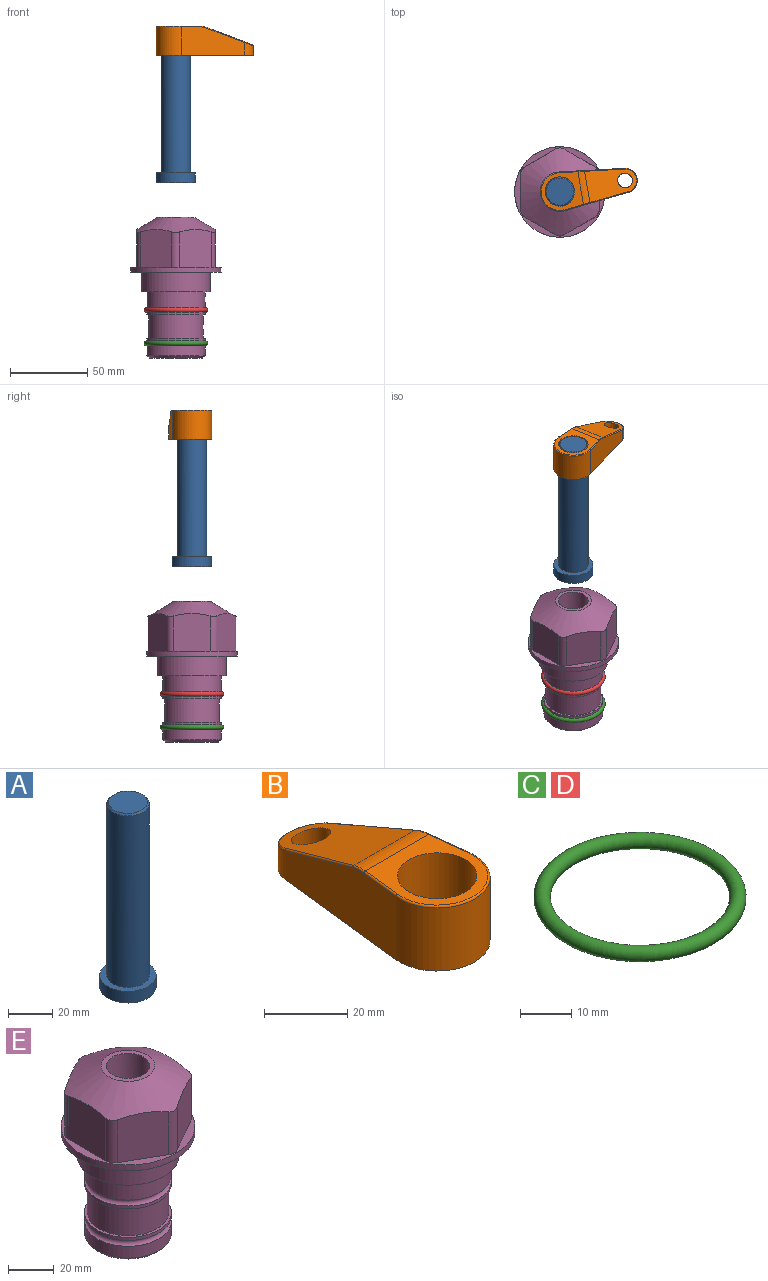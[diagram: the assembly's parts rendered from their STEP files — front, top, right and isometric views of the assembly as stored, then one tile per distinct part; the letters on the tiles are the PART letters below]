
ASSEMBLY  parts=5 mates=3
PART A: 6 faces, bbox 25.4x25.4x101.6 mm
  f0: plane 17.46x17.46mm, normal (0,0,1), area 239.5mm2, adj f5
  f1: plane 25.4x25.4mm, normal (0,0,-1), area 506.7mm2, adj f2
  f2: cylinder r=12.7mm len=25.4mm, axis (0,0,1), area 506.7mm2, adj f1,f3
  f3: plane 25.4x25.4mm, normal (0,0,1), area 221.7mm2, adj f2,f4
  f4: cylinder r=9.53mm len=94.46mm, axis (0,0,1), area 5653mm2, adj f3,f5
  f5: cone r=8.73mm half-angle=45deg, axis (0,0,-1), area 64.4mm2, adj f0,f4
PART B: 44 faces, bbox 27.5x64.5x19.1 mm
  f0: plane 2.3x0.95mm, normal (0,0,-1), area 1mm2, adj f25,f30,f34
  f1: plane 63.5x25.4mm, normal (0,0,-1), area 561.7mm2, adj f2,f3,f4,f5,f6,f7,f19,f20
  f2: cylinder r=12.7mm len=25.4mm, axis (0,0,-1), area 792.2mm2, adj f1,f3,f5,f13
  f3: plane 42.33x18.54mm, normal (0.99,0.11,0), area 647mm2, adj f1,f2,f4,f11,f12,f14
  f4: cylinder r=7.94mm len=15.78mm, axis (0,0,-1), area 158.6mm2, adj f1,f3,f5,f16
  f5: plane 42.33x18.54mm, normal (-0.99,0.11,0), area 647mm2, adj f1,f2,f4,f15,f17,f18
  f6: cylinder r=9.53mm len=19.05mm, axis (0,0,-1), area 1140.1mm2, adj f1,f8
  f7: cylinder r=4.76mm len=10.98mm, axis (0,0,-1), area 276.1mm2, adj f1,f9
  f8: plane 25.83x24.38mm, normal (0,0,1), area 262.2mm2, adj f6,f10,f11,f13,f15
  f9: plane 32.49x20.55mm, normal (0,0.34,0.94), area 489.9mm2, adj f7,f10,f14,f16,f18
  f10: cylinder r=12.7mm len=21.49mm, axis (-1,0,0), area 93.2mm2, adj f8,f9,f12,f17
  f11: cylinder r=0.51mm len=12.34mm, axis (0.11,-0.99,0), area 9.9mm2, adj f3,f8,f12,f13
  f12: bspline ~7.62x1.64mm, area 3.5mm2, adj f3,f10,f11,f14
  f13: torus R=12.19mm, axis (0,0,1), area 33.6mm2, adj f2,f8,f11,f15
  f14: cylinder r=0.51mm len=26.01mm, axis (0.1,-0.93,0.34), area 21.6mm2, adj f3,f9,f12,f16
  f15: cylinder r=0.51mm len=12.34mm, axis (0.11,0.99,0), area 9.9mm2, adj f5,f8,f13,f17
  f16: bspline ~15.78x7.05mm, area 15.7mm2, adj f4,f9,f14,f18
  f17: bspline ~7.62x1.64mm, area 3.5mm2, adj f5,f10,f15,f18
  f18: cylinder r=0.51mm len=26.01mm, axis (0.1,0.93,-0.34), area 21.6mm2, adj f5,f9,f16,f17
  f19: plane 21.6x14.29mm, normal (-0.99,-0.11,0), area 242.6mm2, adj f1,f26,f28,f34,f36,f38
  f20: plane 21.6x14.29mm, normal (0.99,-0.11,0), area 242.6mm2, adj f1,f27,f29,f37,f39,f41
  f21: cylinder r=12.7mm len=14.29mm, axis (0,0,-1), area 173.2mm2, adj f1,f26,f27,f30,f31,f33
  f22: cylinder r=7.94mm len=7.63mm, axis (0,0,-1), area 53.8mm2, adj f1,f28,f29,f42
  f23: plane 2.3x0.95mm, normal (0,0,-1), area 1mm2, adj f25,f33,f37
  f24: plane 17.94x12.32mm, normal (0,-0.34,-0.94), area 191.2mm2, adj f25,f38,f41,f42
  f25: cylinder r=9.53mm len=12.93mm, axis (-1,0,0), area 37.5mm2, adj f0,f23,f24,f31,f36,f39
  f26: cylinder r=1.59mm len=14.29mm, axis (0,0,-1), area 49mm2, adj f1,f19,f21,f32
  f27: cylinder r=1.59mm len=14.29mm, axis (0,0,-1), area 49mm2, adj f1,f20,f21,f35
  f28: cylinder r=1.59mm len=7.28mm, axis (0,0,-1), area 22.1mm2, adj f1,f19,f22,f40
  f29: cylinder r=1.59mm len=7.28mm, axis (0,0,-1), area 22.1mm2, adj f1,f20,f22,f43
  f30: torus R=14.29mm, axis (0,0,1), area 5.8mm2, adj f0,f21,f31,f32
  f31: bspline ~11.06x2.73mm, area 20.8mm2, adj f21,f25,f30,f33
  f32: sphere r=1.59mm, area 5.4mm2, adj f26,f30,f34
  f33: torus R=14.29mm, axis (0,0,1), area 5.8mm2, adj f21,f23,f31,f35
  f34: cylinder r=1.59mm len=1.68mm, axis (-0.11,0.99,0), area 2.4mm2, adj f0,f19,f32,f36
  f35: sphere r=1.59mm, area 5.4mm2, adj f27,f33,f37
  f36: bspline ~5.82x2.33mm, area 7.7mm2, adj f19,f25,f34,f38
  f37: cylinder r=1.59mm len=1.68mm, axis (0.11,0.99,0), area 2.4mm2, adj f20,f23,f35,f39
  f38: cylinder r=1.59mm len=18.33mm, axis (0.1,-0.93,0.34), area 46.7mm2, adj f19,f24,f36,f40
  f39: bspline ~5.82x2.33mm, area 7.7mm2, adj f20,f25,f37,f41
  f40: sphere r=1.59mm, area 3.6mm2, adj f28,f38,f42
  f41: cylinder r=1.59mm len=18.33mm, axis (0.1,0.93,-0.34), area 46.7mm2, adj f20,f24,f39,f43
  f42: bspline ~8.31x1.84mm, area 15.3mm2, adj f22,f24,f40,f43
  f43: sphere r=1.59mm, area 3.6mm2, adj f29,f41,f42
PART C: 1 faces, bbox 44.7x44.7x3.2 mm
  f0: torus R=19.05mm, axis (0,0,1), area 1193.9mm2
PART D: same geometry as C
PART E: 36 faces, bbox 58.7x58.7x91.2 mm
  f0: cylinder r=17.78mm len=35.56mm, axis (0,0,1), area 1670.8mm2, adj f23,f24,f31
  f1: cylinder r=19.05mm len=38.1mm, axis (0,0,1), area 1191.9mm2, adj f26,f27,f30
  f2: plane 58.66x58.66mm, normal (0,0,-1), area 1150.6mm2, adj f3,f28
  f3: cylinder r=29.33mm len=58.66mm, axis (0,0,-1), area 585.1mm2, adj f2,f4
  f4: plane 58.66x58.66mm, normal (0,0,1), area 475.9mm2, adj f3,f5,f6,f7,f8,f9,f10,f11
  f5: plane 24.5x20.32mm, normal (0.5,-0.87,0), area 562.8mm2, adj f4,f15,f16,f17
  f6: plane 24.5x20.32mm, normal (-0.5,-0.87,0), area 562.8mm2, adj f4,f14,f15,f17
  f7: plane 24.5x23.48mm, normal (-1,0,0), area 562.8mm2, adj f4,f13,f14,f17
  f8: plane 24.5x20.32mm, normal (-0.5,0.87,0), area 562.8mm2, adj f4,f12,f13,f17
  f9: plane 24.5x20.32mm, normal (0.5,0.87,0), area 562.8mm2, adj f4,f11,f12,f17
  f10: plane 24.5x23.48mm, normal (1,0,0), area 562.8mm2, adj f4,f11,f16,f17
  f11: cylinder r=5.08mm len=23.01mm, axis (0,0,-1), area 121.2mm2, adj f4,f9,f10,f17
  f12: cylinder r=5.08mm len=23.01mm, axis (0,0,-1), area 121.2mm2, adj f4,f8,f9,f17
  f13: cylinder r=5.08mm len=23.01mm, axis (0,0,-1), area 121.2mm2, adj f4,f7,f8,f17
  f14: cylinder r=5.08mm len=23.01mm, axis (0,0,-1), area 121.2mm2, adj f4,f6,f7,f17
  f15: cylinder r=5.08mm len=23.01mm, axis (0,0,-1), area 121.2mm2, adj f4,f5,f6,f17
  f16: cylinder r=5.08mm len=23.01mm, axis (0,0,-1), area 121.2mm2, adj f4,f5,f10,f17
  f17: cone r=11.73mm half-angle=60deg, axis (0,0,-1), area 2071.8mm2, adj f5,f6,f7,f8,f9,f10,f11,f12
  f18: plane 23.46x23.46mm, normal (0,0,1), area 147.4mm2, adj f17,f35
  f19: plane 34.93x34.93mm, normal (0,0,-1), area 958mm2, adj f29
  f20: cylinder r=19.05mm len=38.1mm, axis (0,0,1), area 760.1mm2, adj f21,f29
  f21: torus R=19.05mm, axis (0,0,1), area 565.3mm2, adj f20,f22
  f22: cylinder r=19.05mm len=38.1mm, axis (0,0,1), area 190mm2, adj f21,f23
  f23: plane 38.1x38.1mm, normal (0,0,1), area 146.9mm2, adj f0,f22
  f24: plane 38.1x38.1mm, normal (0,0,-1), area 146.9mm2, adj f0,f25
  f25: cylinder r=19.05mm len=38.1mm, axis (0,0,1), area 190mm2, adj f24,f26
  f26: torus R=19.05mm, axis (0,0,1), area 565.3mm2, adj f1,f25
  f27: plane 44.45x44.45mm, normal (0,0,-1), area 411.7mm2, adj f1,f28
  f28: cylinder r=22.23mm len=44.45mm, axis (0,0,1), area 1773.5mm2, adj f2,f27
  f29: cone r=19.05mm half-angle=45deg, axis (0,0,1), area 257.5mm2, adj f19,f20
  f30: cylinder r=3.17mm len=6.75mm, axis (-1,0,0), area 128mm2, adj f1,f33
  f31: cylinder r=3.17mm len=6.35mm, axis (-1,0,0), area 102.5mm2, adj f0,f33
  f32: plane 25.4x25.4mm, normal (0,0,1), area 506.7mm2, adj f33
  f33: cylinder r=12.7mm len=66.42mm, axis (0,0,-1), area 5236.2mm2, adj f30,f31,f32,f34
  f34: cone r=9.53mm half-angle=30deg, axis (0,0,-1), area 443.4mm2, adj f33,f35
  f35: cylinder r=9.53mm len=19.05mm, axis (0,0,-1), area 849mm2, adj f18,f34
PLACE A rot(axis=(0,0,1),9.6deg) t=(0,0,85.98)mm
PLACE B rot(axis=(0,0,-1),80.4deg) t=(0,0,140.59)mm
PLACE C t=(0,0,-21.59)mm
PLACE D at identity
PLACE E at identity fixed
MATE fastened C.f0 <-> E.f0  axis (0,0,1) through (0,0,-46.1)mm
MATE cylindrical A.f2 <-> E.f0  axis (0,0,1) through (0,0,111.62)mm
MATE fastened B.f2 <-> A.f2  axis (0,0,1) through (0,0,159.64)mm
